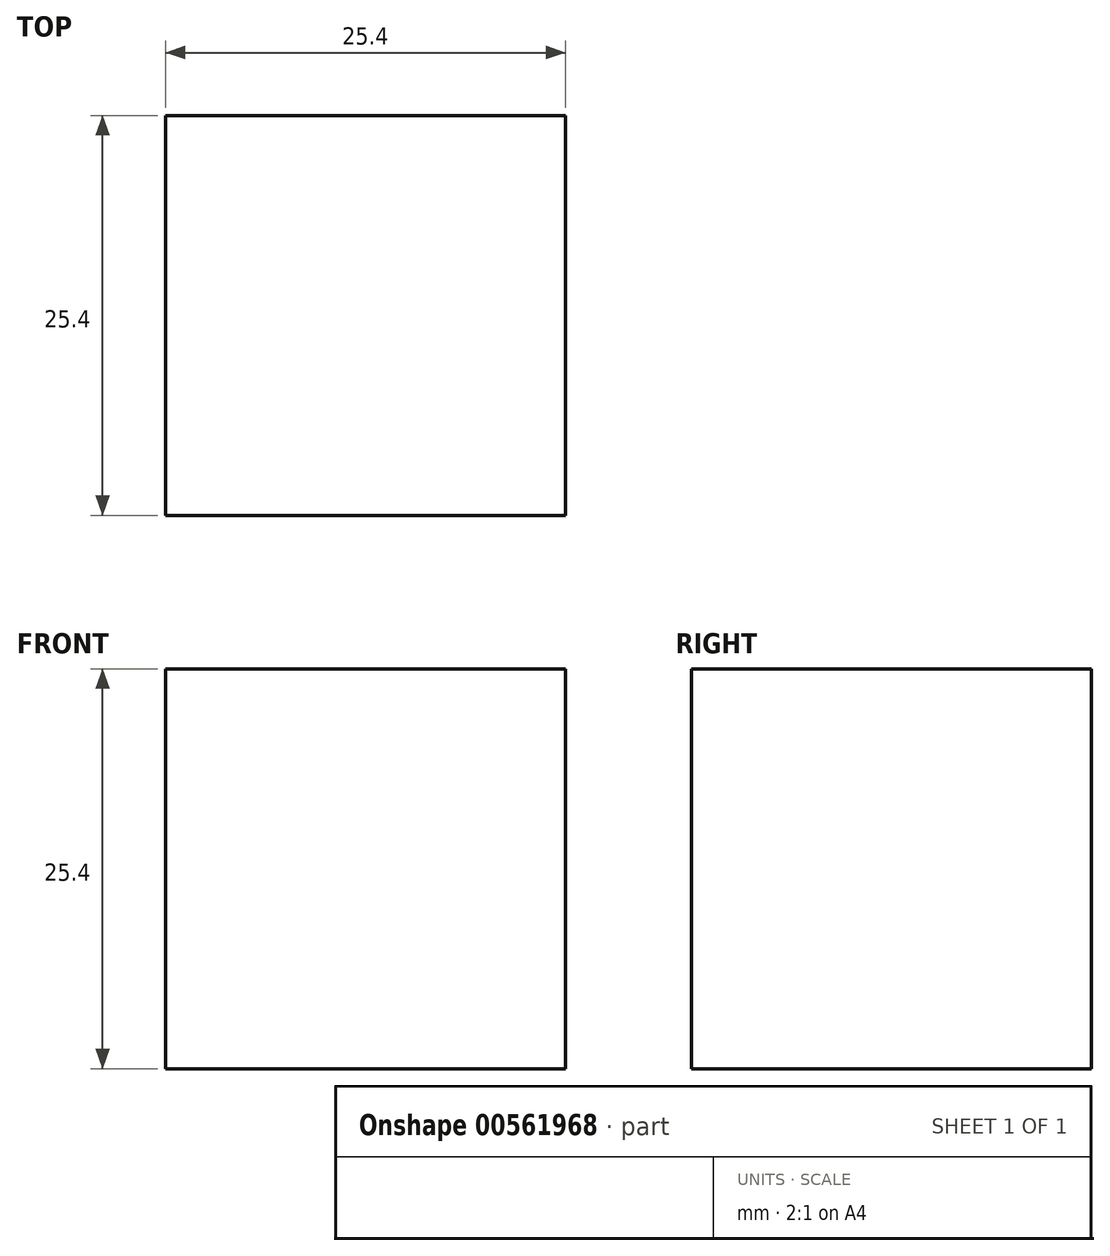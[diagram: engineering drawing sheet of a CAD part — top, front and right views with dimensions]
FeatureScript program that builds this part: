
annotation { "Feature Type Name" : "Feature", "Feature Type Description" : "" }
export const myFeature = defineFeature(function(context is Context, id is Id, definition is map)
    precondition{}
    {
        {
            var Q0;
            Q0=qCreatedBy(makeId("Front.planeOp"),FACE);
            var sketch = newSketch(context, id + "F0", { "sketchPlane" : qUnion([Q0])});
            skLineSegment(sketch, "E0.bottom", {"start": v(-31.66, 25.4) * mm, "end": v(-6.26, 25.4) * mm});
            skLineSegment(sketch, "E0.top", {"start": v(-31.66, 0) * mm, "end": v(-6.26, 0) * mm});
            skLineSegment(sketch, "E0.left", {"start": v(-31.66, 25.4) * mm, "end": v(-31.66, 0) * mm});
            skLineSegment(sketch, "E0.right", {"start": v(-6.26, 25.4) * mm, "end": v(-6.26, 0) * mm});
            skSolve(sketch);
        }
        {
            var Q0;
            Q0=makeQuery(id+"F0.imprint","IMPRINT",FACE,{"disambiguationData":[TD([[makeQuery(id+"F0.imprint","IMPRINT",EDGE,{"derivedFrom":sQuery(id+"F0.wireOp",EDGE,"E0.bottom")}),-1.0]])]});
            extrude(context, id + "F1", {"entities" : qUnion([Q0]), "depth" : 25.4 * mm, "offsetDistance" : 25.4 * mm});
        }
    });
